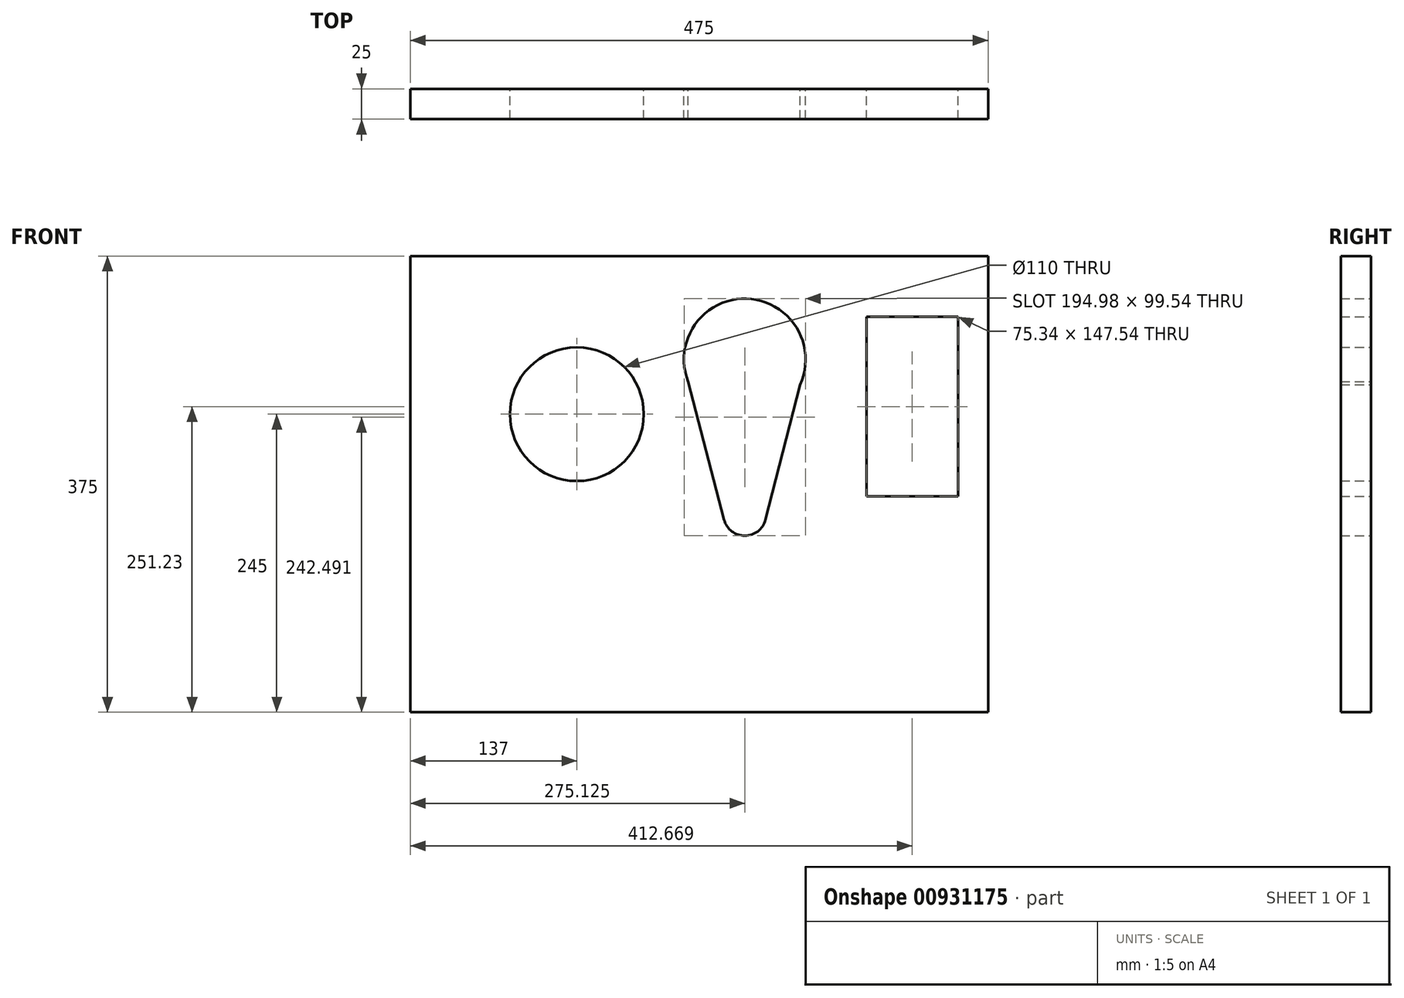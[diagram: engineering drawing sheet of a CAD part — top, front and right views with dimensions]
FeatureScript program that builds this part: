
annotation { "Feature Type Name" : "Feature", "Feature Type Description" : "" }
export const myFeature = defineFeature(function(context is Context, id is Id, definition is map)
    precondition{}
    {
        {
            var Q0;
            Q0=qCreatedBy(makeId("Front.planeOp"),FACE);
            var sketch = newSketch(context, id + "F0", { "sketchPlane" : qUnion([Q0])});
            skLineSegment(sketch, "E0.bottom", {"start": v(-237.5, 187.5) * mm, "end": v(237.5, 187.5) * mm});
            skLineSegment(sketch, "E0.top", {"start": v(-237.5, -187.5) * mm, "end": v(237.5, -187.5) * mm});
            skLineSegment(sketch, "E0.left", {"start": v(-237.5, 187.5) * mm, "end": v(-237.5, -187.5) * mm});
            skLineSegment(sketch, "E0.right", {"start": v(237.5, 187.5) * mm, "end": v(237.5, -187.5) * mm});
            skPoint(sketch, "E0.middle", {"position": v(0, 0) * mm});
            skCircle(sketch, "E1", {"center": v(-100.5, 57.5) * mm, "radius": 55 * mm});
            skLineSegment(sketch, "E2.bottom", {"start": v(137.5, 137.5) * mm, "end": v(212.84, 137.5) * mm});
            skLineSegment(sketch, "E2.top", {"start": v(137.5, -10.04) * mm, "end": v(212.84, -10.04) * mm});
            skLineSegment(sketch, "E2.left", {"start": v(137.5, 137.5) * mm, "end": v(137.5, -10.04) * mm});
            skLineSegment(sketch, "E2.right", {"start": v(212.84, 137.5) * mm, "end": v(212.84, -10.04) * mm});
            skCircle(sketch, "E3", {"center": v(37.5, 102.5) * mm, "radius": 50 * mm});
            skCircle(sketch, "E4", {"center": v(37.5, -25) * mm, "radius": 17.5 * mm});
            skLineSegment(sketch, "E5", {"start": v(-12.04, 95.72) * mm, "end": v(20.57, -29.41) * mm});
            skLineSegment(sketch, "E6", {"start": v(87.36, 98.77) * mm, "end": v(54.45, -29.35) * mm});
            skSolve(sketch);
        }
        {
            var Q0;
            Q0=makeQuery(id+"F0.imprint","IMPRINT",FACE,{"disambiguationData":[TD([[makeQuery(id+"F0.imprint","IMPRINT",EDGE,{"derivedFrom":sQuery(id+"F0.wireOp",EDGE,"E0.bottom")}),-1.0]])]});
            extrude(context, id + "F1", {"entities" : qUnion([Q0]), "depth" : 25 * mm, "offsetDistance" : 25 * mm});
        }
    });
